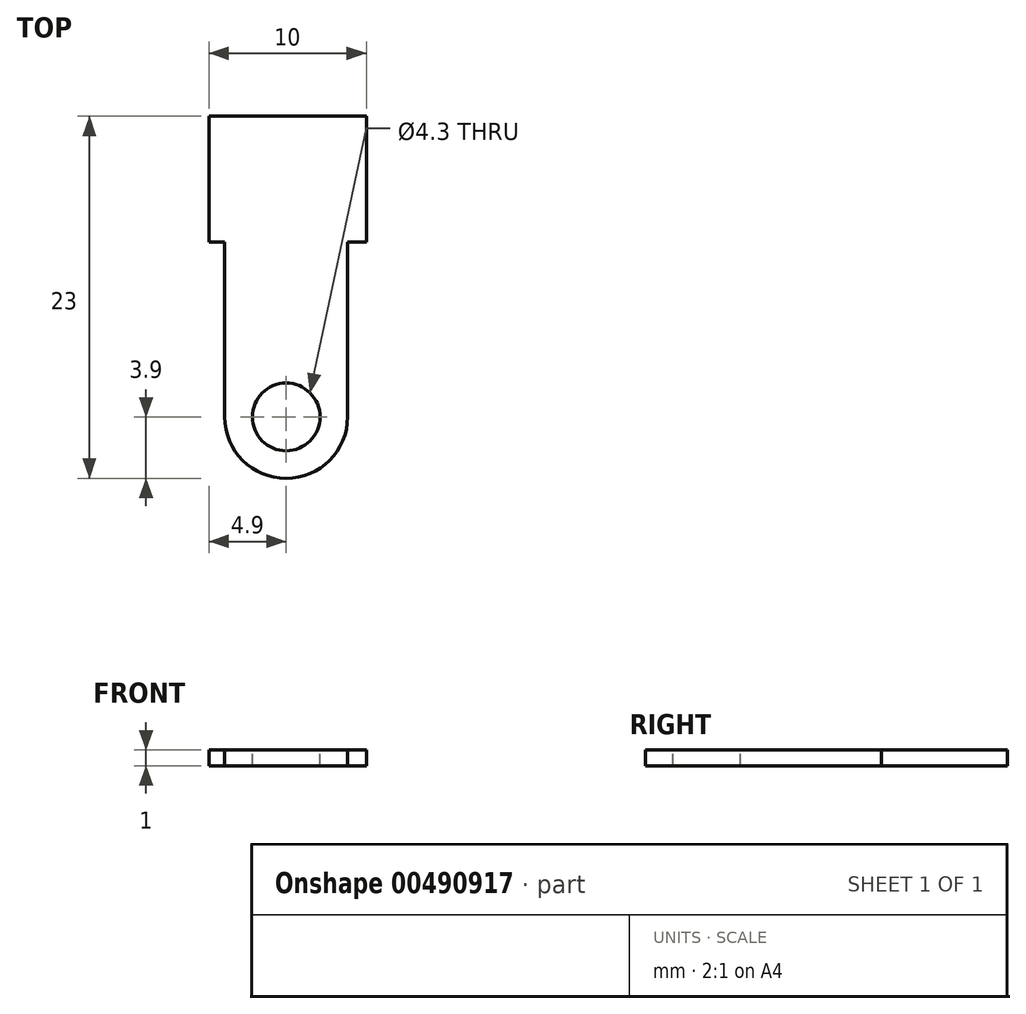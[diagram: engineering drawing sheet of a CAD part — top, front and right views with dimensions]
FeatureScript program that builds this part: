
annotation { "Feature Type Name" : "Feature", "Feature Type Description" : "" }
export const myFeature = defineFeature(function(context is Context, id is Id, definition is map)
    precondition{}
    {
        {
            var Q0;
            Q0=qCreatedBy(makeId("Front.planeOp"),FACE);
            var sketch = newSketch(context, id + "F0", { "sketchPlane" : qUnion([Q0])});
            skLineSegment(sketch, "E0.bottom", {"start": v(3.9, 23) * mm, "end": v(3.9, 23) * mm});
            skLineSegment(sketch, "E0.top", {"start": v(0, 0) * mm, "end": v(7.8, 0) * mm});
            skLineSegment(sketch, "E0.left", {"start": v(0, 19.1) * mm, "end": v(0, 0) * mm});
            skLineSegment(sketch, "E0.right", {"start": v(7.8, 19.1) * mm, "end": v(7.8, 0) * mm});
            skLineSegment(sketch, "E1.bottom", {"start": v(-1, 8) * mm, "end": v(9, 8) * mm});
            skLineSegment(sketch, "E1.top", {"start": v(-1, 0) * mm, "end": v(9, 0) * mm});
            skLineSegment(sketch, "E1.left", {"start": v(-1, 8) * mm, "end": v(-1, 0) * mm});
            skLineSegment(sketch, "E1.right", {"start": v(9, 8) * mm, "end": v(9, 0) * mm});
            skPoint(sketch, "E2.visualSharp", {"position": v(0, 23) * mm});
            skArc(sketch, "E2.filletArc", {"start": v(3.9, 23) * mm, "mid": v(1.14, 21.86) * mm, "end": v(0, 19.1) * mm});
            skPoint(sketch, "E3.visualSharp", {"position": v(7.8, 23) * mm});
            skArc(sketch, "E3.filletArc", {"start": v(7.8, 19.1) * mm, "mid": v(6.66, 21.86) * mm, "end": v(3.9, 23) * mm});
            skCircle(sketch, "E4", {"center": v(3.9, 19.1) * mm, "radius": 2.15 * mm});
            skSolve(sketch);
        }
        {
            var Q0;
            {var subQ0=sQuery(id+"F0.wireOp",EDGE,"E2.filletArc");Q0=makeQuery(id+"F0.imprint","IMPRINT",FACE,{"disambiguationData":[TD([[makeQuery(id+"F0.imprint","IMPRINT",EDGE,{"derivedFrom":subQ0}),1.0]])]});}
            var Q1;
            {var subQ0=sQuery(id+"F0.wireOp",EDGE,"E1.top");var subQ1=sQuery(id+"F0.wireOp",EDGE,"E0.left");var subQ2=makeQuery(id+"F0.imprint","INTERSECT",VERTEX,{"derivedFrom":[subQ1,subQ0]});Q1=makeQuery(id+"F0.imprint","IMPRINT",FACE,{"disambiguationData":[TD([[makeQuery(id+"F0.imprint","IMPRINT",EDGE,{"disambiguationData":[TD([[subQ2,1.0]])],"derivedFrom":subQ1}),1.0]])]});}
            var Q2;
            {var subQ5=sQuery(id+"F0.wireOp",EDGE,"E1.right");Q2=makeQuery(id+"F0.imprint","IMPRINT",FACE,{"disambiguationData":[TD([[makeQuery(id+"F0.imprint","IMPRINT",EDGE,{"derivedFrom":subQ5}),-1.0]])]});}
            var Q3;
            {var subQ5=sQuery(id+"F0.wireOp",EDGE,"E1.left");Q3=makeQuery(id+"F0.imprint","IMPRINT",FACE,{"disambiguationData":[TD([[makeQuery(id+"F0.imprint","IMPRINT",EDGE,{"derivedFrom":subQ5}),1.0]])]});}
            extrude(context, id + "F1", {"entities" : qUnion([Q0, Q1, Q2, Q3]), "depth" : 1 * mm});
        }
        {
            var Q0;
            Q0=makeQuery(id+"F1.opExtrude","SWEPT_BODY",BODY,{"disambiguationData":[OSD([sQuery(id+"F0.wireOp",EDGE,"E0.left"),sQuery(id+"F0.wireOp",EDGE,"E0.right"),sQuery(id+"F0.wireOp",EDGE,"E1.bottom"),sQuery(id+"F0.wireOp",EDGE,"E1.top"),sQuery(id+"F0.wireOp",EDGE,"E1.left"),sQuery(id+"F0.wireOp",EDGE,"E1.right"),sQuery(id+"F0.wireOp",EDGE,"E2.filletArc"),sQuery(id+"F0.wireOp",EDGE,"E3.filletArc"),sQuery(id+"F0.wireOp",EDGE,"E4")])]});
            var Q1;
            Q1=makeQuery(id+"F1.opExtrude","CAP_EDGE",EDGE,{"disambiguationData":[OSD([sQuery(id+"F0.wireOp",EDGE,"E1.top")])],"isStart":false});
            transform(context, id + "F2", {"entities" : qUnion([Q0]), "transformType" : TransformType.ROTATION, "transformAxis" : qUnion([Q1]), "angle" : 90 * degree, "makeCopy" : false});
        }
    });
